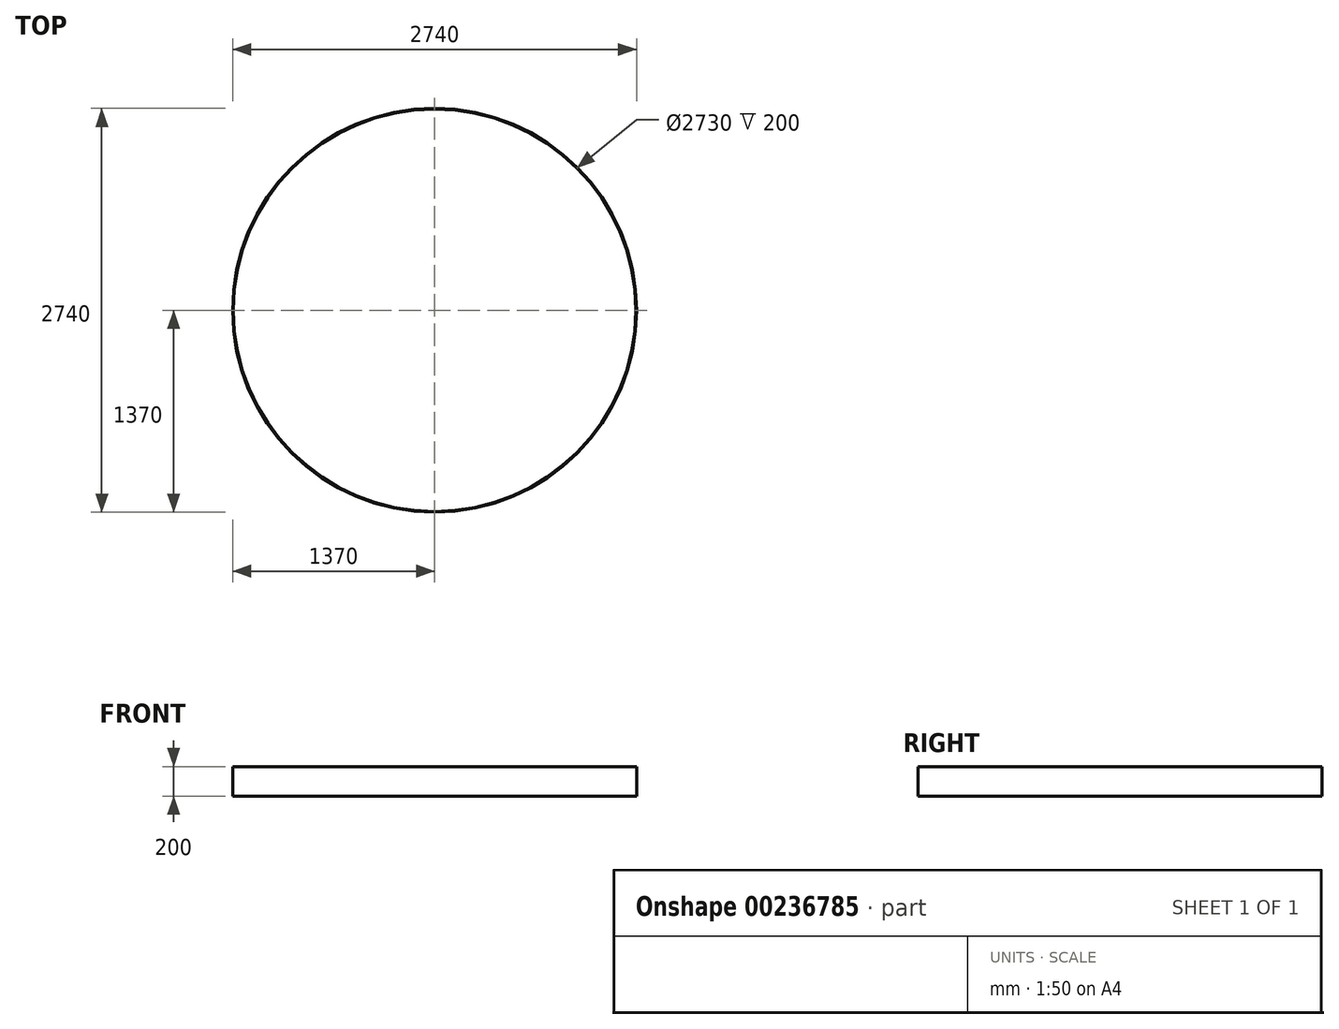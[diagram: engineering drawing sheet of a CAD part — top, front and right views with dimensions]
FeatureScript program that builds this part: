
annotation { "Feature Type Name" : "Feature", "Feature Type Description" : "" }
export const myFeature = defineFeature(function(context is Context, id is Id, definition is map)
    precondition{}
    {
        {
            var Q0;
            Q0=qCreatedBy(makeId("Top.planeOp"),FACE);
            var sketch = newSketch(context, id + "F0", { "sketchPlane" : qUnion([Q0])});
            skCircle(sketch, "E0", {"center": v(0, 0) * mm, "radius": 1365 * mm});
            skCircle(sketch, "E1", {"center": v(0, 0) * mm, "radius": 1370 * mm});
            skLineSegment(sketch, "E2", {"start": v(-860, 843.27) * mm, "end": v(1670, 843.27) * mm, "construction": true});
            skLineSegment(sketch, "E3", {"start": v(1670, 843.27) * mm, "end": v(1670, 318.27) * mm, "construction": true});
            skLineSegment(sketch, "E4", {"start": v(1670, 318.27) * mm, "end": v(-1190, 318.27) * mm, "construction": true});
            skLineSegment(sketch, "E5", {"start": v(1670, -311.73) * mm, "end": v(-1190, -311.73) * mm, "construction": true});
            skLineSegment(sketch, "E6", {"start": v(1670, -836.73) * mm, "end": v(-860, -836.73) * mm, "construction": true});
            skLineSegment(sketch, "E7", {"start": v(1670, -836.73) * mm, "end": v(1670, 318.27) * mm, "construction": true});
            skPoint(sketch, "E8", {"position": v(0, 318.27) * mm});
            skPoint(sketch, "E9", {"position": v(-880, 318.27) * mm});
            skPoint(sketch, "E10", {"position": v(920, 318.27) * mm});
            skPoint(sketch, "E11", {"position": v(-280, 318.27) * mm});
            skPoint(sketch, "E12", {"position": v(-760, -311.73) * mm});
            skPoint(sketch, "E13", {"position": v(-260, -311.73) * mm});
            skPoint(sketch, "E14", {"position": v(240, -311.73) * mm});
            skPoint(sketch, "E15", {"position": v(889.44, -311.73) * mm});
            skPoint(sketch, "E16", {"position": v(300, -836.73) * mm});
            skPoint(sketch, "E17", {"position": v(-300, -836.73) * mm});
            skPoint(sketch, "E18", {"position": v(-300, 843.27) * mm});
            skPoint(sketch, "E19", {"position": v(0, 843.27) * mm});
            skPoint(sketch, "E20", {"position": v(300, 843.27) * mm});
            skCircle(sketch, "E21", {"center": v(-300, 843.27) * mm, "radius": 480 * mm, "construction": true});
            skCircle(sketch, "E22", {"center": v(-880, 318.27) * mm, "radius": 480 * mm, "construction": true});
            skCircle(sketch, "E23", {"center": v(-280, 318.27) * mm, "radius": 480 * mm, "construction": true});
            skCircle(sketch, "E24", {"center": v(920, 318.27) * mm, "radius": 480 * mm, "construction": true});
            skCircle(sketch, "E25", {"center": v(889.44, -311.73) * mm, "radius": 480 * mm, "construction": true});
            skCircle(sketch, "E26", {"center": v(240, -311.73) * mm, "radius": 480 * mm, "construction": true});
            skCircle(sketch, "E27", {"center": v(-260, -311.73) * mm, "radius": 480 * mm, "construction": true});
            skCircle(sketch, "E28", {"center": v(-300, -836.73) * mm, "radius": 480 * mm, "construction": true});
            skCircle(sketch, "E29", {"center": v(-760, -311.73) * mm, "radius": 480 * mm, "construction": true});
            skPoint(sketch, "E30", {"position": v(320, 318.27) * mm});
            skCircle(sketch, "E31", {"center": v(320, 318.27) * mm, "radius": 480 * mm, "construction": true});
            skLineSegment(sketch, "E32", {"start": v(0, 1498.76) * mm, "end": v(0, 0) * mm, "construction": true});
            skLineSegment(sketch, "E33", {"start": v(0, 0) * mm, "end": v(0, -1907.6) * mm, "construction": true});
            skLineSegment(sketch, "E34", {"start": v(1827.6, 0) * mm, "end": v(-1540.68, 0) * mm, "construction": true});
            skCircle(sketch, "E35", {"center": v(300, -836.73) * mm, "radius": 480 * mm, "construction": true});
            skCircle(sketch, "E36", {"center": v(300, 843.27) * mm, "radius": 480 * mm, "construction": true});
            skSolve(sketch);
        }
        {
            var Q0;
            Q0=makeQuery(id+"F0.imprint","IMPRINT",FACE,{"disambiguationData":[TD([[makeQuery(id+"F0.imprint","IMPRINT",EDGE,{"derivedFrom":sQuery(id+"F0.wireOp",EDGE,"E0")}),-1.0]])]});
            extrude(context, id + "F1", {"entities" : qUnion([Q0]), "depth" : 200 * mm, "offsetDistance" : 25 * mm});
        }
    });
